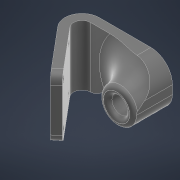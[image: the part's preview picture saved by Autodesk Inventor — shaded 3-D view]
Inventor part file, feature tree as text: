
AUTODESK INVENTOR PART (.ipt)
format: ipt  version: 2021 (Build 250183000, 183)  size: 265,216 bytes
history: native  units: mm
features: extrude x5, other x5, fillet x5, projected_geometry x3
ambient origin geometry x8: Origin, YZ Plane, XZ Plane, XY Plane, X Axis, Y Axis, Z Axis, Center Point
bodies: Solid1 (feature_tree)
feature tree (18):
  extrude  "base"  Depth=4.0mm
  other  "camera_holes_sketch"
  other  "rod_support_sketch"
  extrude  "base_cutout"  Depth=4.0mm
  extrude  "rod_support"  Depth=8.726646mm
  fillet  "base_cutout_fillet"  Radius=28.0mm
  extrude  "camera_holes"  Depth=4.0mm
  fillet  "camera_plate_bottom"  Radius=34.0mm
  fillet  "rod_holder_draft"  Radius=28.0mm
  other  "rod_holes_plane"
  extrude  "rod_holes"  Depth=20.0mm
  fillet  "Fillet4"  Radius=2.2mm
  fillet  "Fillet5"  Radius=4.0mm
  other  "base_sketch"
  projected_geometry  "Projected Loop1"
  projected_geometry  "Projected Loop2"
  other  "rod_holes_sketch"
  projected_geometry  "Projected Loop3"
